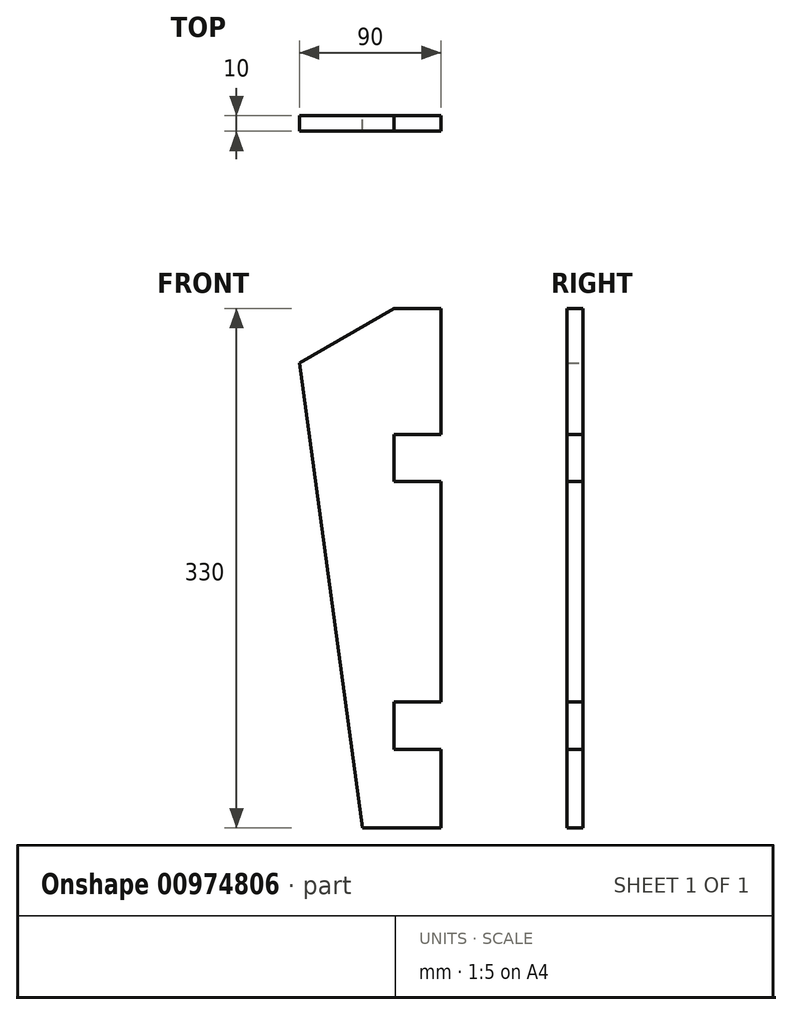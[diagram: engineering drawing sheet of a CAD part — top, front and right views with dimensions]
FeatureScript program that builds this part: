
annotation { "Feature Type Name" : "Feature", "Feature Type Description" : "" }
export const myFeature = defineFeature(function(context is Context, id is Id, definition is map)
    precondition{}
    {
        {
            var Q0;
            Q0=qCreatedBy(makeId("Front.planeOp"),FACE);
            var sketch = newSketch(context, id + "F0", { "sketchPlane" : qUnion([Q0])});
            skLineSegment(sketch, "E0", {"start": v(0, 0) * mm, "end": v(30, 0) * mm});
            skLineSegment(sketch, "E1", {"start": v(30, 0) * mm, "end": v(30, 80) * mm});
            skLineSegment(sketch, "E2", {"start": v(30, 80) * mm, "end": v(0, 80) * mm});
            skLineSegment(sketch, "E3", {"start": v(0, 80) * mm, "end": v(-60, 45.36) * mm});
            skLineSegment(sketch, "E4", {"start": v(-60, 45.36) * mm, "end": v(-20, -250) * mm});
            skLineSegment(sketch, "E5", {"start": v(0, 0) * mm, "end": v(0, -30) * mm});
            skLineSegment(sketch, "E6", {"start": v(0, -30) * mm, "end": v(30, -30) * mm});
            skLineSegment(sketch, "E7", {"start": v(30, -30) * mm, "end": v(30, -170) * mm});
            skLineSegment(sketch, "E8", {"start": v(30, -170) * mm, "end": v(0, -170) * mm});
            skLineSegment(sketch, "E9", {"start": v(0, -170) * mm, "end": v(0, -200) * mm});
            skLineSegment(sketch, "E10", {"start": v(0, -200) * mm, "end": v(30, -200) * mm});
            skLineSegment(sketch, "E11", {"start": v(30, -200) * mm, "end": v(30, -250) * mm});
            skLineSegment(sketch, "E12", {"start": v(30, -250) * mm, "end": v(-20, -250) * mm});
            skLineSegment(sketch, "E13", {"start": v(0, 80) * mm, "end": v(0, 0) * mm, "construction": true});
            skLineSegment(sketch, "E14", {"start": v(-60, 45.36) * mm, "end": v(0, 45.36) * mm, "construction": true});
            skSolve(sketch);
        }
        {
            var Q0;
            Q0 = qSketchRegion(id + "F0", true);
            extrude(context, id + "F1", {"entities" : qUnion([Q0]), "depth" : 10 * mm, "offsetDistance" : 25 * mm});
        }
    });
